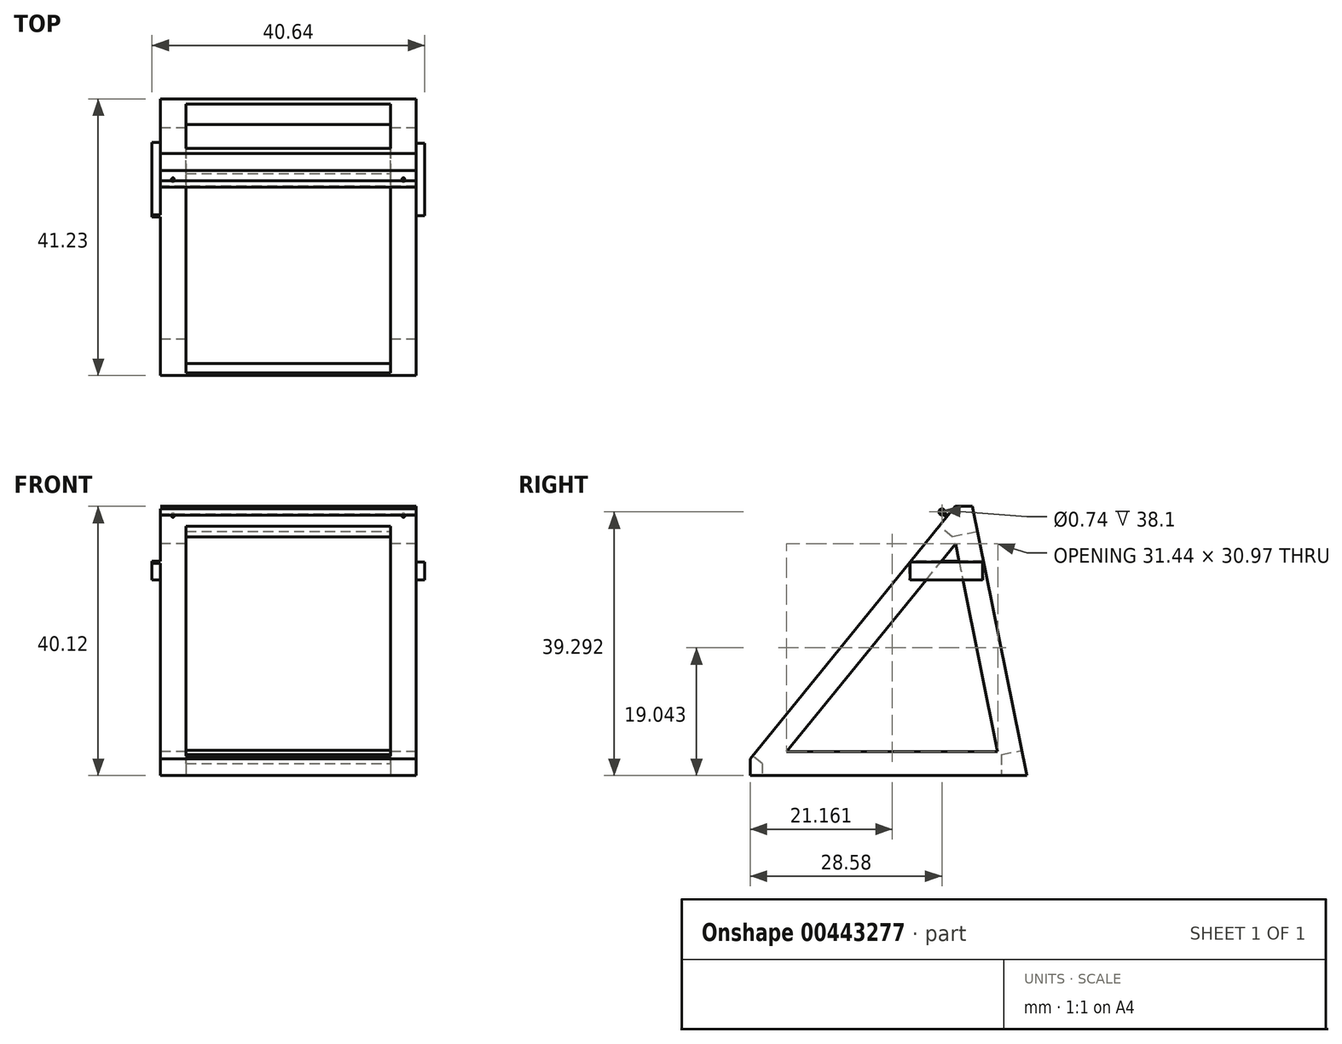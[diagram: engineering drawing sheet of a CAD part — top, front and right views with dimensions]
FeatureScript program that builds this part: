
annotation { "Feature Type Name" : "Feature", "Feature Type Description" : "" }
export const myFeature = defineFeature(function(context is Context, id is Id, definition is map)
    precondition{}
    {
        {
            var Q0;
            Q0=qCreatedBy(makeId("Right.planeOp"),FACE);
            var sketch = newSketch(context, id + "F0", { "sketchPlane" : qUnion([Q0])});
            skLineSegment(sketch, "E0", {"start": v(0, 0) * mm, "end": v(-31.44, 0) * mm});
            skLineSegment(sketch, "E1", {"start": v(-31.44, 0) * mm, "end": v(-6.29, 30.97) * mm});
            skLineSegment(sketch, "E2", {"start": v(-6.29, 30.97) * mm, "end": v(0, 0) * mm});
            skLineSegment(sketch, "E3.0", {"start": v(-38.9, -3.56) * mm, "end": v(-4.3, 39.05) * mm});
            skLineSegment(sketch, "E3.1", {"start": v(4.35, -3.56) * mm, "end": v(-38.9, -3.56) * mm});
            skLineSegment(sketch, "E3.2", {"start": v(-4.3, 39.05) * mm, "end": v(4.35, -3.56) * mm});
            skSolve(sketch);
        }
        {
            var Q0;
            Q0=makeQuery(id+"F0.imprint","IMPRINT",FACE,{"disambiguationData":[TD([[makeQuery(id+"F0.imprint","IMPRINT",EDGE,{"derivedFrom":sQuery(id+"F0.wireOp",EDGE,"E0")}),1.0]])]});
            extrude(context, id + "F1", {"entities" : qUnion([Q0]), "endBound" : BoundingType.SYMMETRIC, "depth" : 38.1 * mm});
        }
        {
            var Q0;
            Q0=makeQuery(id+"F1.opExtrude","CAP_FACE",FACE,{"disambiguationData":[OSD([sQuery(id+"F0.wireOp",EDGE,"E0"),sQuery(id+"F0.wireOp",EDGE,"E1"),sQuery(id+"F0.wireOp",EDGE,"E2"),sQuery(id+"F0.wireOp",EDGE,"E3.0"),sQuery(id+"F0.wireOp",EDGE,"E3.1"),sQuery(id+"F0.wireOp",EDGE,"E3.2")])],"isStart":false});
            var sketch = newSketch(context, id + "F2", { "sketchPlane" : qUnion([Q0])});
            skLineSegment(sketch, "E4", {"start": v(-3.8, 36.56) * mm, "end": v(-6.33, 36.56) * mm});
            skLineSegment(sketch, "E5.bottom", {"start": v(-14.22, 26.85) * mm, "end": v(-1.8, 26.85) * mm});
            skLineSegment(sketch, "E5.top", {"start": v(-14.22, 24.52) * mm, "end": v(-1.8, 24.52) * mm});
            skLineSegment(sketch, "E5.left", {"start": v(-14.22, 26.85) * mm, "end": v(-14.22, 24.52) * mm});
            skLineSegment(sketch, "E5.right", {"start": v(-1.8, 26.85) * mm, "end": v(-1.8, 24.52) * mm});
            skSolve(sketch);
        }
        {
            var Q0;
            {var subQ0=sQuery(id+"F2.wireOp",EDGE,"E4");Q0=makeQuery(id+"F2.imprint","IMPRINT",FACE,{"disambiguationData":[TD([[makeQuery(id+"F2.imprint","IMPRINT",EDGE,{"derivedFrom":subQ0}),-1.0]])]});}
            extrude(context, id + "F3", {"entities" : qUnion([Q0]), "operationType" : NewBodyOperationType.REMOVE, "oppositeDirection" : true, "depth" : 50.8 * mm});
        }
        {
            var Q0;
            Q0=makeQuery(id+"F1.opExtrude","CAP_FACE",FACE,{"disambiguationData":[OSD([sQuery(id+"F0.wireOp",EDGE,"E0"),sQuery(id+"F0.wireOp",EDGE,"E1"),sQuery(id+"F0.wireOp",EDGE,"E2"),sQuery(id+"F0.wireOp",EDGE,"E3.0"),sQuery(id+"F0.wireOp",EDGE,"E3.1"),sQuery(id+"F0.wireOp",EDGE,"E3.2")])],"isStart":false});
            var sketch = newSketch(context, id + "F4", { "sketchPlane" : qUnion([Q0])});
            skLineSegment(sketch, "E6.bottom", {"start": v(-13.07, 28.25) * mm, "end": v(-2.25, 28.25) * mm});
            skLineSegment(sketch, "E6.top", {"start": v(-13.07, 25.62) * mm, "end": v(-2.25, 25.62) * mm});
            skLineSegment(sketch, "E6.left", {"start": v(-13.07, 28.25) * mm, "end": v(-13.07, 25.62) * mm});
            skLineSegment(sketch, "E6.right", {"start": v(-2.25, 28.25) * mm, "end": v(-2.25, 25.62) * mm});
            skSolve(sketch);
        }
        {
            var Q0;
            Q0=makeQuery(id+"F1.opExtrude","CAP_FACE",FACE,{"disambiguationData":[OSD([sQuery(id+"F0.wireOp",EDGE,"E0"),sQuery(id+"F0.wireOp",EDGE,"E1"),sQuery(id+"F0.wireOp",EDGE,"E2"),sQuery(id+"F0.wireOp",EDGE,"E3.0"),sQuery(id+"F0.wireOp",EDGE,"E3.1"),sQuery(id+"F0.wireOp",EDGE,"E3.2")])],"isStart":true});
            var sketch = newSketch(context, id + "F5", { "sketchPlane" : qUnion([Q0])});
            skLineSegment(sketch, "E7.bottom", {"start": v(2.14, 28.42) * mm, "end": v(13.22, 28.42) * mm});
            skLineSegment(sketch, "E7.top", {"start": v(2.14, 25.62) * mm, "end": v(13.22, 25.62) * mm});
            skLineSegment(sketch, "E7.left", {"start": v(2.14, 28.42) * mm, "end": v(2.14, 25.62) * mm});
            skLineSegment(sketch, "E7.right", {"start": v(13.22, 28.42) * mm, "end": v(13.22, 25.62) * mm});
            skSolve(sketch);
        }
        {
            var Q0;
            {var subQ0=sQuery(id+"F5.wireOp",EDGE,"E7.left");Q0=makeQuery(id+"F5.imprint","IMPRINT",FACE,{"disambiguationData":[TD([[makeQuery(id+"F5.imprint","IMPRINT",EDGE,{"derivedFrom":subQ0}),1.0]])]});}
            var Q1;
            {var subQ0=sQuery(id+"F5.wireOp",EDGE,"E7.bottom");var subQ1=makeQuery(id+"F1.opExtrude","CAP_EDGE",EDGE,{"disambiguationData":[OSD([sQuery(id+"F0.wireOp",EDGE,"E2")])],"isStart":true});var subQ2=makeQuery(id+"F5.imprint","INTERSECT",VERTEX,{"derivedFrom":[subQ1,subQ0]});Q1=makeQuery(id+"F5.imprint","IMPRINT",FACE,{"disambiguationData":[TD([[makeQuery(id+"F5.imprint","IMPRINT",EDGE,{"disambiguationData":[TD([[subQ2,-1.0]])],"derivedFrom":subQ0}),-1.0]])]});}
            var Q2;
            {var subQ0=sQuery(id+"F5.wireOp",EDGE,"E7.bottom");var subQ7=makeQuery(id+"F1.opExtrude","CAP_EDGE",EDGE,{"disambiguationData":[OSD([sQuery(id+"F0.wireOp",EDGE,"E3.0")])],"isStart":true});var subQ9=makeQuery(id+"F5.imprint","INTERSECT",VERTEX,{"derivedFrom":[subQ7,subQ0]});Q2=makeQuery(id+"F5.imprint","IMPRINT",FACE,{"disambiguationData":[TD([[makeQuery(id+"F5.imprint","IMPRINT",EDGE,{"disambiguationData":[TD([[subQ9,1.0]])],"derivedFrom":subQ0}),-1.0]])]});}
            extrude(context, id + "F6", {"entities" : qUnion([Q0, Q1, Q2]), "operationType" : NewBodyOperationType.ADD, "depth" : 1.27 * mm});
        }
        {
            var Q0;
            {var subQ0=sQuery(id+"F4.wireOp",EDGE,"E6.left");Q0=makeQuery(id+"F4.imprint","IMPRINT",FACE,{"disambiguationData":[TD([[makeQuery(id+"F4.imprint","IMPRINT",EDGE,{"derivedFrom":subQ0}),1.0]])]});}
            var Q1;
            {var subQ0=sQuery(id+"F4.wireOp",EDGE,"E6.right");Q1=makeQuery(id+"F4.imprint","IMPRINT",FACE,{"disambiguationData":[TD([[makeQuery(id+"F4.imprint","IMPRINT",EDGE,{"derivedFrom":subQ0}),-1.0]])]});}
            var Q2;
            {var subQ0=sQuery(id+"F4.wireOp",EDGE,"E6.bottom");var subQ1=makeQuery(id+"F1.opExtrude","CAP_EDGE",EDGE,{"disambiguationData":[OSD([sQuery(id+"F0.wireOp",EDGE,"E1")])],"isStart":false});var subQ2=makeQuery(id+"F4.imprint","INTERSECT",VERTEX,{"derivedFrom":[subQ1,subQ0]});Q2=makeQuery(id+"F4.imprint","IMPRINT",FACE,{"disambiguationData":[TD([[makeQuery(id+"F4.imprint","IMPRINT",EDGE,{"disambiguationData":[TD([[subQ2,-1.0]])],"derivedFrom":subQ0}),-1.0]])]});}
            extrude(context, id + "F7", {"entities" : qUnion([Q0, Q1, Q2]), "operationType" : NewBodyOperationType.ADD, "depth" : 1.27 * mm});
        }
        {
            var Q0;
            {var subQ0=sQuery(id+"F0.wireOp",EDGE,"E3.0");Q0=makeQuery(id+"F6.boolean.opBoolean","MERGE",FACE,{"derivedFrom":[makeQuery(id+"F1.opExtrude","SWEPT_FACE",FACE,{"disambiguationData":[OSD([subQ0])]}),makeQuery(id+"F6.opExtrude","SWEPT_FACE",FACE,{"disambiguationData":[OSD([subQ0])]})]});}
            var sketch = newSketch(context, id + "F8", { "sketchPlane" : qUnion([Q0])});
            skLineSegment(sketch, "E8.0", {"start": v(-15.24, -23.48) * mm, "end": v(-15.24, 13.46) * mm});
            skLineSegment(sketch, "E8.1", {"start": v(15.24, -23.48) * mm, "end": v(-15.24, -23.48) * mm});
            skLineSegment(sketch, "E8.2", {"start": v(-15.24, 13.9) * mm, "end": v(-15.24, 20.58) * mm});
            skLineSegment(sketch, "E8.3", {"start": v(-15.24, 20.58) * mm, "end": v(15.24, 20.58) * mm});
            skLineSegment(sketch, "E8.4", {"start": v(15.24, 13.69) * mm, "end": v(15.24, 20.58) * mm});
            skLineSegment(sketch, "E8.5", {"start": v(15.24, -23.48) * mm, "end": v(15.24, 13.69) * mm});
            skLineSegment(sketch, "E9", {"start": v(-15.24, 13.46) * mm, "end": v(-15.24, 13.9) * mm});
            skLineSegment(sketch, "E10", {"start": v(15.24, 13.69) * mm, "end": v(15.24, 13.83) * mm});
            skSolve(sketch);
        }
        {
            var Q0;
            Q0=makeQuery(id+"F8.imprint","IMPRINT",FACE,{"disambiguationData":[TD([[makeQuery(id+"F8.imprint","IMPRINT",EDGE,{"derivedFrom":sQuery(id+"F8.wireOp",EDGE,"E8.0")}),-1.0]])]});
            extrude(context, id + "F9", {"entities" : qUnion([Q0]), "operationType" : NewBodyOperationType.REMOVE, "oppositeDirection" : true, "depth" : 4.06 * mm});
        }
        {
            var Q0;
            Q0=makeQuery(id+"F1.opExtrude","SWEPT_FACE",FACE,{"disambiguationData":[OSD([sQuery(id+"F0.wireOp",EDGE,"E3.2")])]});
            var sketch = newSketch(context, id + "F10", { "sketchPlane" : qUnion([Q0])});
            skLineSegment(sketch, "E11.0", {"start": v(-15.24, 32.77) * mm, "end": v(-15.24, -0.54) * mm});
            skLineSegment(sketch, "E11.1", {"start": v(15.24, 32.77) * mm, "end": v(-15.24, 32.77) * mm});
            skLineSegment(sketch, "E11.2", {"start": v(-15.24, -0.54) * mm, "end": v(15.24, -0.54) * mm});
            skLineSegment(sketch, "E11.3", {"start": v(15.24, 28.27) * mm, "end": v(15.24, -0.54) * mm});
            skLineSegment(sketch, "E11.4", {"start": v(15.24, 32.77) * mm, "end": v(15.24, 28.27) * mm});
            skSolve(sketch);
        }
        {
            var Q0;
            Q0=makeQuery(id+"F10.imprint","IMPRINT",FACE,{"disambiguationData":[TD([[makeQuery(id+"F10.imprint","IMPRINT",EDGE,{"derivedFrom":sQuery(id+"F10.wireOp",EDGE,"E11.0")}),1.0]])]});
            extrude(context, id + "F11", {"entities" : qUnion([Q0]), "operationType" : NewBodyOperationType.REMOVE, "oppositeDirection" : true, "depth" : 3.8 * mm});
        }
        {
            var Q0;
            Q0=makeQuery(id+"F1.opExtrude","SWEPT_FACE",FACE,{"disambiguationData":[OSD([sQuery(id+"F0.wireOp",EDGE,"E3.1")])]});
            var sketch = newSketch(context, id + "F12", { "sketchPlane" : qUnion([Q0])});
            skLineSegment(sketch, "E12.0", {"start": v(15.24, 35.1) * mm, "end": v(-15.24, 35.1) * mm});
            skLineSegment(sketch, "E12.1", {"start": v(15.24, -0.54) * mm, "end": v(15.24, 35.1) * mm});
            skLineSegment(sketch, "E12.2", {"start": v(15.24, -0.54) * mm, "end": v(-15.24, -0.54) * mm});
            skLineSegment(sketch, "E12.3", {"start": v(-15.24, -0.54) * mm, "end": v(-15.24, 35.1) * mm});
            skSolve(sketch);
        }
        {
            var Q0;
            Q0=makeQuery(id+"F12.imprint","IMPRINT",FACE,{"disambiguationData":[TD([[makeQuery(id+"F12.imprint","IMPRINT",EDGE,{"derivedFrom":sQuery(id+"F12.wireOp",EDGE,"E12.0")}),1.0]])]});
            extrude(context, id + "F13", {"entities" : qUnion([Q0]), "operationType" : NewBodyOperationType.REMOVE, "oppositeDirection" : true, "depth" : 3.8 * mm});
        }
        {
            var Q0;
            {var subQ0=sQuery(id+"F0.wireOp",EDGE,"E3.0");Q0=makeQuery(id+"F6.boolean.opBoolean","MERGE",FACE,{"derivedFrom":[makeQuery(id+"F1.opExtrude","SWEPT_FACE",FACE,{"disambiguationData":[OSD([subQ0])]}),makeQuery(id+"F6.opExtrude","SWEPT_FACE",FACE,{"disambiguationData":[OSD([subQ0])]})]});}
            var sketch = newSketch(context, id + "F14", { "sketchPlane" : qUnion([Q0])});
            skLineSegment(sketch, "E13", {"start": v(15.24, 20.58) * mm, "end": v(15.24, 24.39) * mm, "construction": true});
            skLineSegment(sketch, "E14", {"start": v(15.24, 20.58) * mm, "end": v(19.05, 20.58) * mm, "construction": true});
            skPoint(sketch, "E14.endSnap0", {"position": v(19.05, 19.04) * mm});
            skLineSegment(sketch, "E15", {"start": v(-15.24, 20.58) * mm, "end": v(-19.05, 20.58) * mm, "construction": true});
            skLineSegment(sketch, "E16", {"start": v(-15.24, 20.58) * mm, "end": v(-15.24, 24.39) * mm, "construction": true});
            skLineSegment(sketch, "E17", {"start": v(15.24, 22.48) * mm, "end": v(17.14, 22.48) * mm, "construction": true});
            skLineSegment(sketch, "E18", {"start": v(17.14, 22.48) * mm, "end": v(17.14, 20.58) * mm, "construction": true});
            skLineSegment(sketch, "E19", {"start": v(-15.24, 22.48) * mm, "end": v(-17.2, 22.48) * mm, "construction": true});
            skLineSegment(sketch, "E20", {"start": v(-17.2, 22.48) * mm, "end": v(-17.2, 20.58) * mm, "construction": true});
            skCircle(sketch, "E21", {"center": v(-17.2, 22.48) * mm, "radius": 0.2 * mm});
            skCircle(sketch, "E22", {"center": v(17.14, 22.48) * mm, "radius": 0.2 * mm});
            skSolve(sketch);
        }
        {
            var Q0;
            Q0 = qSketchRegion(id + "F14", true);
            extrude(context, id + "F15", {"entities" : qUnion([Q0]), "operationType" : NewBodyOperationType.ADD, "depth" : 1.02 * mm});
        }
        {
            var Q0;
            Q0=makeQuery(id+"F1.opExtrude","CAP_FACE",FACE,{"disambiguationData":[OSD([sQuery(id+"F0.wireOp",EDGE,"E0"),sQuery(id+"F0.wireOp",EDGE,"E1"),sQuery(id+"F0.wireOp",EDGE,"E2"),sQuery(id+"F0.wireOp",EDGE,"E3.0"),sQuery(id+"F0.wireOp",EDGE,"E3.1"),sQuery(id+"F0.wireOp",EDGE,"E3.2")])],"isStart":false});
            var sketch = newSketch(context, id + "F16", { "sketchPlane" : qUnion([Q0])});
            skLineSegment(sketch, "E23", {"start": v(-36.88, -3.56) * mm, "end": v(-36.88, -1.05) * mm});
            skSolve(sketch);
        }
        {
            var Q0;
            Q0 = qSketchRegion(id + "F16", true);
            var Q1;
            {var subQ0=sQuery(id+"F16.wireOp",EDGE,"E23");Q1=makeQuery(id+"F16.imprint","IMPRINT",FACE,{"disambiguationData":[TD([[makeQuery(id+"F16.imprint","IMPRINT",EDGE,{"derivedFrom":subQ0}),1.0]])]});}
            extrude(context, id + "F17", {"entities" : qUnion([Q0, Q1]), "operationType" : NewBodyOperationType.REMOVE, "oppositeDirection" : true, "depth" : 50.8 * mm});
        }
        {
            var Q0;
            {var subQ0=sQuery(id+"F0.wireOp",EDGE,"E3.0");var subQ1=sQuery(id+"F0.wireOp",EDGE,"E2");var subQ4=sQuery(id+"F0.wireOp",EDGE,"E1");var subQ5=sQuery(id+"F0.wireOp",EDGE,"E3.2");var subQ6=makeQuery(id+"F1.opExtrude","CAP_FACE",FACE,{"disambiguationData":[OSD([sQuery(id+"F0.wireOp",EDGE,"E0"),subQ4,subQ1,subQ0,sQuery(id+"F0.wireOp",EDGE,"E3.1"),subQ5])],"isStart":true});Q0=makeQuery(id+"F6.boolean.opBoolean","SPLIT",FACE,{"disambiguationData":[TD([makeQuery(id+"F3.boolean.opBoolean","COPY",FACE,{"derivedFrom":makeQuery(id+"F3.opExtrude","SWEPT_FACE",FACE,{"disambiguationData":[OSD([sQuery(id+"F2.wireOp",EDGE,"E4")])]})})])],"derivedFrom":subQ6});}
            var sketch = newSketch(context, id + "F18", { "sketchPlane" : qUnion([Q0])});
            skLineSegment(sketch, "E24", {"start": v(7.52, 35.1) * mm, "end": v(8.89, 36.2) * mm, "construction": true});
            skCircle(sketch, "E25", {"center": v(8.3, 35.73) * mm, "radius": 0.47 * mm});
            skCircle(sketch, "E26.0", {"center": v(8.3, 35.73) * mm, "radius": 0.37 * mm});
            skSolve(sketch);
        }
        {
            var Q0;
            Q0=makeQuery(id+"F18.imprint","IMPRINT",FACE,{"disambiguationData":[TD([[makeQuery(id+"F18.imprint","IMPRINT",EDGE,{"derivedFrom":sQuery(id+"F18.wireOp",EDGE,"E25")}),1.0]])]});
            extrude(context, id + "F19", {"entities" : qUnion([Q0]), "operationType" : NewBodyOperationType.ADD, "oppositeDirection" : true, "depth" : 38.1 * mm});
        }
        {
            var Q0;
            Q0=makeQuery(id+"F18.imprint","IMPRINT",FACE,{"disambiguationData":[TD([[makeQuery(id+"F18.imprint","IMPRINT",EDGE,{"derivedFrom":sQuery(id+"F18.wireOp",EDGE,"E26.0")}),1.0]])]});
            extrude(context, id + "F20", {"entities" : qUnion([Q0]), "operationType" : NewBodyOperationType.REMOVE, "oppositeDirection" : true, "depth" : 42.88 * mm});
        }
    });
